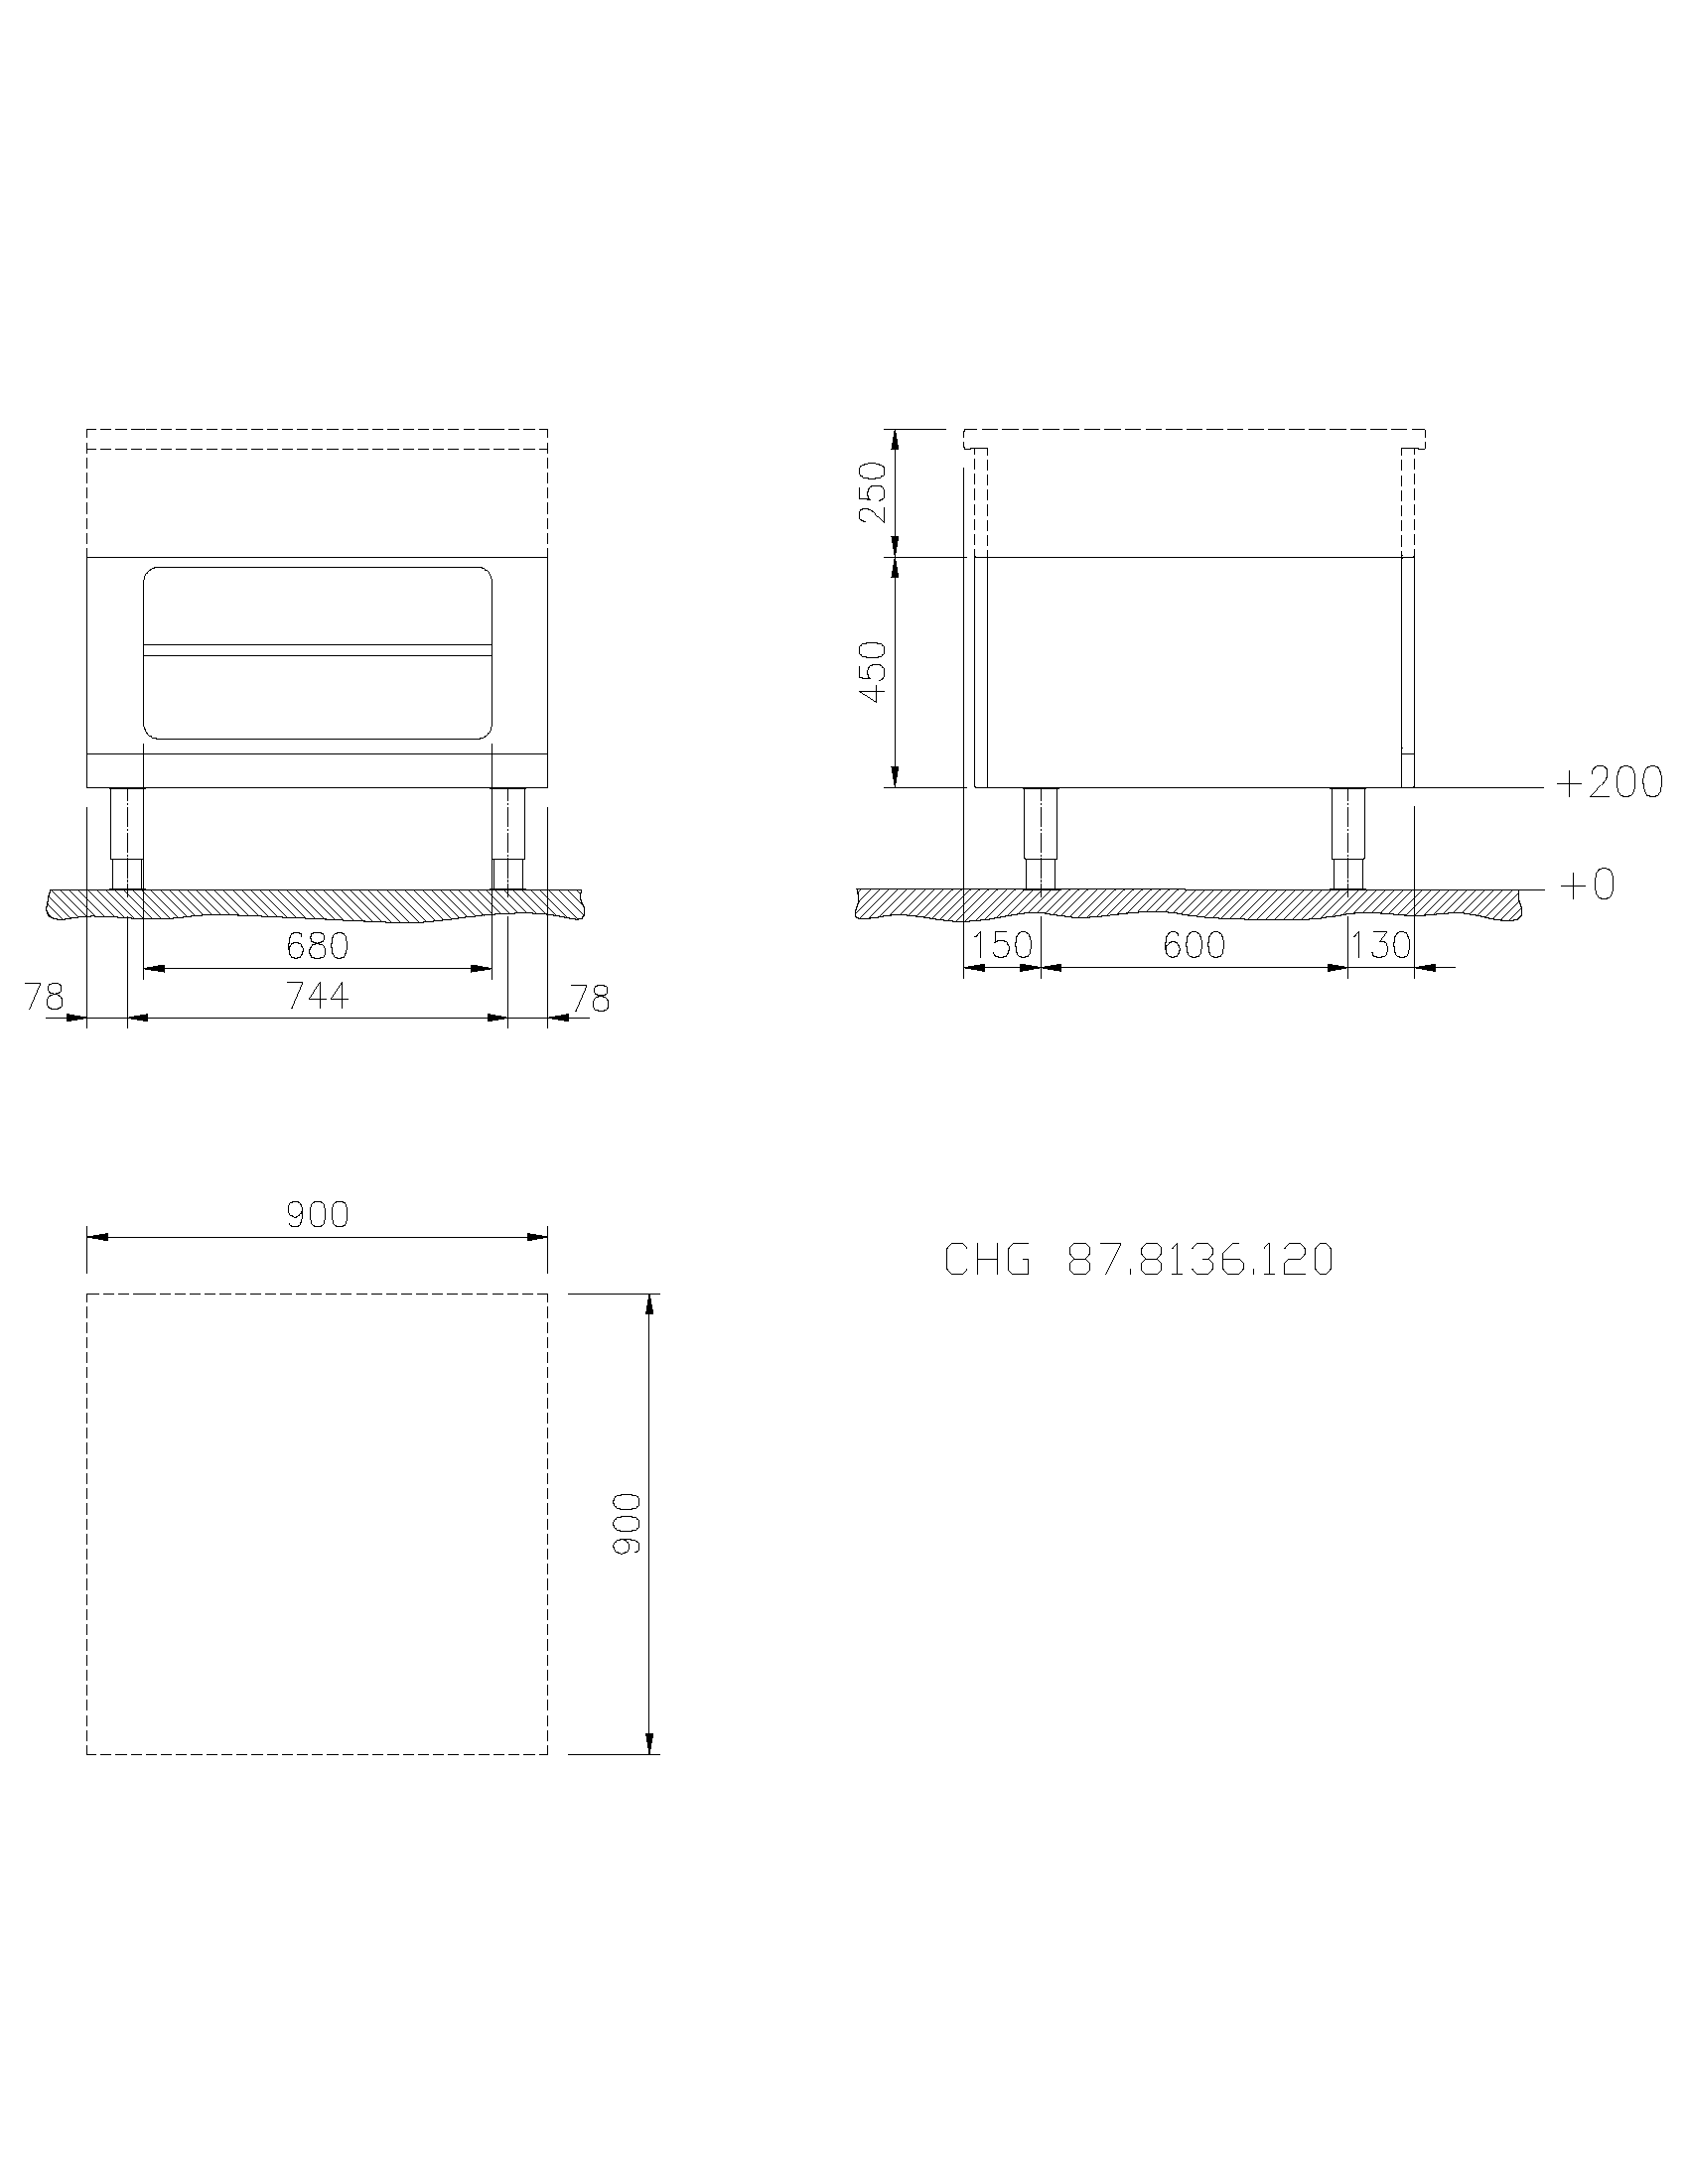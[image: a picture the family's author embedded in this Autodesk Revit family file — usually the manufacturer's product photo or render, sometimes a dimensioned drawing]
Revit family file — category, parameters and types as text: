
# Revit family: QF_ELECTROLUXPROFESSIONAL_589852_MCJQEAE1DM
name_source: partatom
category: Attrezzature speciali
units: mm (PartAtom-declared; Revit-internal decimal feet)

## family parameters
Basato su piano di lavoro = No
Condiviso = No
Punto di calcolo locali = No
Quota connettore circolare = Usa diametro
Sempre verticale = Sì
Taglio con vuoti quando caricato = No
Tipo di parte = Normale

## types (1)
- Standard
    Accessory = Sì
    Cold Water Size = 0"
    Compressed Air Pressure = 0.00 psi
    Compressed Air Size = 0"
    Compressed Air Volume = 0 GPM
    Condensate Return Size = 0"
    Cycle = 50 Hz
    Depth Actual = 900 mm  [stored 2.95276 ft]
    Descrizione = FULL IND,OPEN,H3,2Z,1S,500X900X700-MAR
    Direct Waste Size = 0"
    Gas Input Pressure = 0.0
    Gas KW = 0
    Gas Size = 0"
    HP = 18.8 HP
    Height Actual = 700 mm  [stored 2.29659 ft]
    Hot Water Size = 0"
    Item Number = 589852
    Length Actual = 500 mm  [stored 1.64042 ft]
    Modello = MCJQEAE1DM
    Phase = 3
    Produttore = Electrolux Professional
    Prospetto di default = 0 mm  [stored 0 ft]
    Refrigerant Compressor Remote = Sì
    Refrigeration Liquid Line Size = 0 mm  [stored 0 ft]
    Refrigeration Suction Line Size = 0 mm  [stored 0 ft]
    Steam Consumption per Hour = 0
    Steam Supply Maximum Pressure = 0.00 psi
    Steam Supply Minimum Pressure = 0.00 psi
    Steam Supply Size = 0"
    URL = https://www.electroluxprofessional.com
    URL Manufacturer = https://www.electroluxprofessional.com
    Volts = 440 V
    Watts = 14000 W
    Weight = 51.00 kg

note: source unit labels omitted for Gas Input Pressure — the stored unit's dimension contradicts the parameter name (converter mislabeling)

note: [stored X ft] marks values corroborated as IEEE doubles in the binary element streams (Revit-internal decimal feet)

## geometry (parser evidence)
native form markers: Blend x13, Sweep x12
no freeform markers — native parametric forms only
